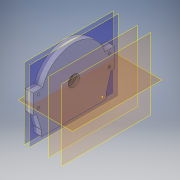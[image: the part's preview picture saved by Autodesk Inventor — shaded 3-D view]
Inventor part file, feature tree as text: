
AUTODESK INVENTOR PART (.ipt)
format: ipt  version: 2019 (Build 230136000, 136)  size: 513,536 bytes
history: native  units: mm
features: sketch x28, extrude x21, mirror x13, plane x12, projected_geometry x11, fillet x4, hole x3, other x2
ambient origin geometry x8: Origin, YZ Plane, XZ Plane, XY Plane, X Axis, Y Axis, Z Axis, Center Point
bodies: Body1 (feature_tree)
feature tree (94):
  other  "實體1"
  extrude  "擠出1"  Depth=123.43mm
  plane  "工作平面2"
  extrude  "擠出3"  Depth=160.0mm
  plane  "工作平面3"
  sketch  "草圖5"
  extrude  "擠出4"  Depth=120.0mm TaperAngle=0.0deg
  extrude  "擠出5"  [1 undecoded]
  plane  "工作平面4"
  extrude  "擠出7"  Depth=130.0mm
  plane  "工作平面5"
  extrude  "擠出9"  Depth=15.0mm TaperAngle=0.0deg
  extrude  "擠出10"  [1 undecoded]
  extrude  "擠出11"  Depth=140.0mm
  extrude  "擠出12"  Depth=10.0mm TaperAngle=0.0deg
  mirror  "鏡射1"
  fillet  "圓角2"  Radius=10.0mm
  fillet  "圓角3"  Radius=10.0mm
  sketch  "草圖16"
  plane  "工作平面7"
  mirror  "鏡射2"
  fillet  "圓角5"  [1 undecoded]
  fillet  "圓角6"  Radius=10.0mm
  plane  "工作平面8"
  plane  "工作平面9"
  sketch  "草圖20"
  sketch  "草圖21"
  extrude  "擠出15"  [1 undecoded]
  plane  "工作平面10"
  extrude  "擠出16"  Depth=10.0mm
  extrude  "擠出17"  Depth=10.0mm TaperAngle=0.0deg
  plane  "工作平面11"
  extrude  "擠出19"  Depth=10.0mm TaperAngle=0.0deg
  extrude  "擠出20"  Depth=160.0mm
  mirror  "鏡射3"
  mirror  "鏡射4"
  extrude  "擠出21"  Depth=80.0mm
  mirror  "鏡射7"
  plane  "工作平面15"
  mirror  "鏡射9"
  hole  "孔2"  [1 undecoded]
  mirror  "鏡射10"
  mirror  "鏡射11"
  hole  "孔3"  [1 undecoded]
  mirror  "鏡射12"
  mirror  "鏡射13"
  extrude  "擠出22"  Depth=160.0mm
  extrude  "擠出23"  Depth=120.0mm TaperAngle=0.0deg
  extrude  "擠出24"  Depth=120.0mm TaperAngle=0.0deg
  extrude  "擠出25"  Depth=25.0mm
  extrude  "擠出27"  Depth=20.0mm
  extrude  "擠出28"  Depth=2.0mm
  mirror  "鏡射14"
  plane  "工作平面17"
  hole  "孔4"  [1 undecoded]
  mirror  "鏡射15"
  mirror  "鏡射16"
  other  "分割1"
  sketch  "草圖1"
  sketch  "草圖4"
  sketch  "草圖6"
  sketch  "草圖7"
  projected_geometry  "投影迴路1"
  sketch  "草圖9"
  projected_geometry  "投影迴路4"
  sketch  "草圖11"
  sketch  "草圖12"
  projected_geometry  "投影迴路6"
  sketch  "草圖13"
  projected_geometry  "投影迴路7"
  sketch  "草圖14"
  plane  "工作平面6"
  sketch  "草圖17"
  projected_geometry  "投影迴路8"
  sketch  "草圖24"
  projected_geometry  "投影迴路11"
  sketch  "草圖25"
  sketch  "草圖26"
  sketch  "草圖27"
  sketch  "草圖28"
  sketch  "草圖29"
  projected_geometry  "投影迴路12"
  sketch  "草圖30"
  sketch  "草圖31"
  sketch  "草圖32"
  projected_geometry  "投影迴路13"
  projected_geometry  "投影迴路14"
  projected_geometry  "投影迴路15"
  sketch  "草圖33"
  sketch  "草圖34"
  sketch  "草圖35"
  projected_geometry  "投影迴路16"
  sketch  "草圖36"
  sketch  "草圖37"
note: 7 required parameter values undecoded (feature->parameter linkage not recoverable at this tier; creation-order binding heuristic only, values carry confidence <= 0.55)
